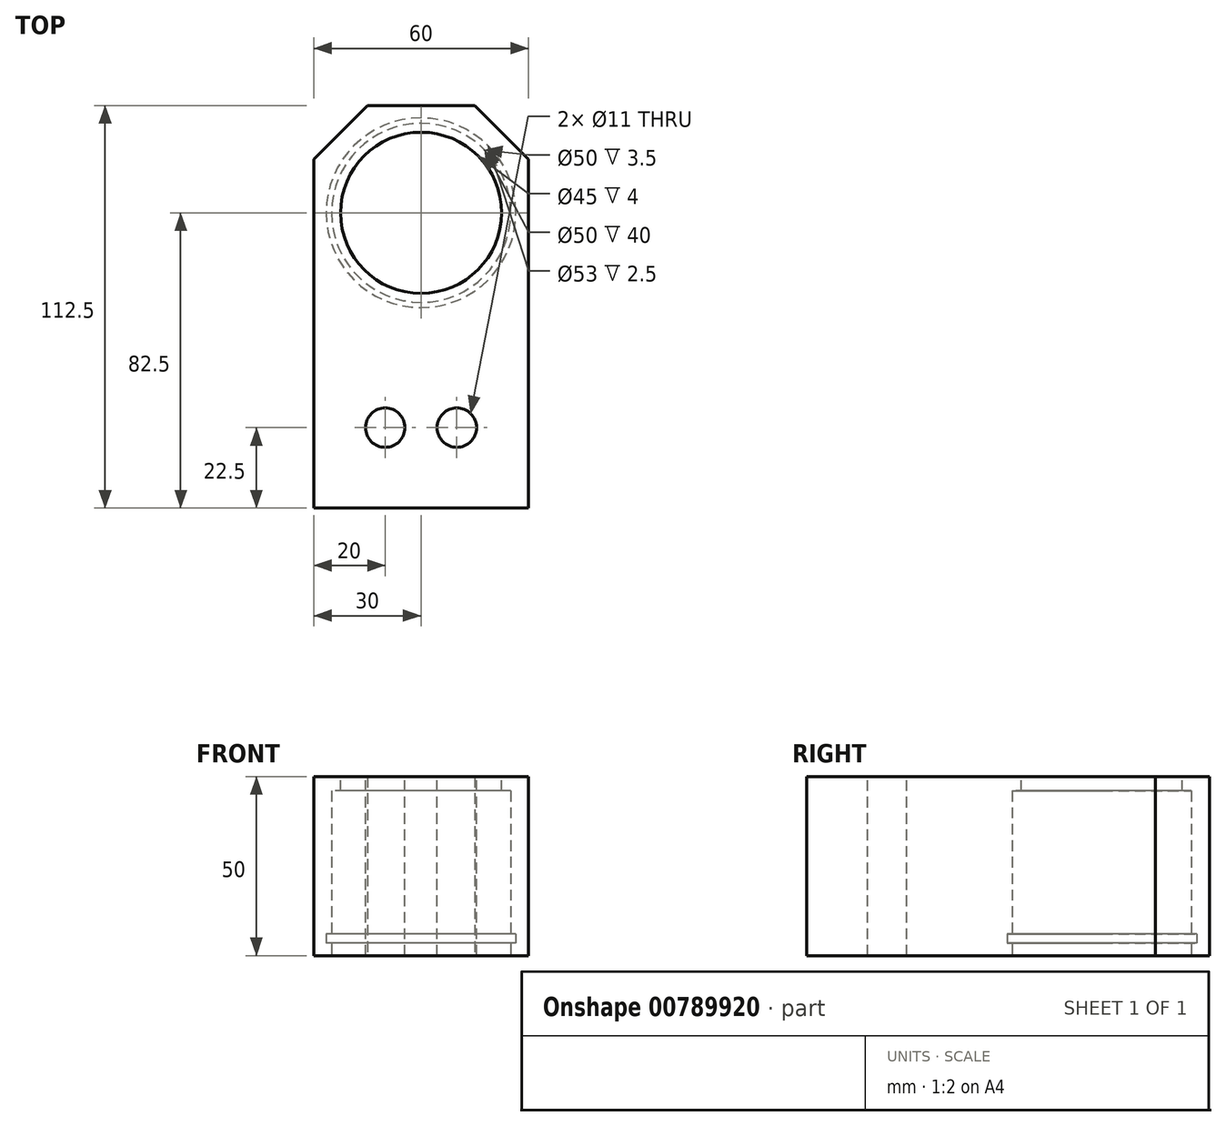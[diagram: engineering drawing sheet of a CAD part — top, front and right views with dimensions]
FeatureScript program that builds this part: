
annotation { "Feature Type Name" : "Feature", "Feature Type Description" : "" }
export const myFeature = defineFeature(function(context is Context, id is Id, definition is map)
    precondition{}
    {
        {
            var Q0;
            Q0=qCreatedBy(makeId("Top.planeOp"),FACE);
            var sketch = newSketch(context, id + "F0", { "sketchPlane" : qUnion([Q0])});
            skLineSegment(sketch, "E0.bottom", {"start": v(-15, 30) * mm, "end": v(15, 30) * mm});
            skLineSegment(sketch, "E0.top", {"start": v(-30, -82.5) * mm, "end": v(30, -82.5) * mm});
            skLineSegment(sketch, "E0.left", {"start": v(-30, 15) * mm, "end": v(-30, -82.5) * mm});
            skLineSegment(sketch, "E0.right", {"start": v(30, 15) * mm, "end": v(30, -82.5) * mm});
            skLineSegment(sketch, "E1", {"start": v(-30, 15) * mm, "end": v(-15, 30) * mm});
            skLineSegment(sketch, "E2.MirrorCS", {"start": v(30, 15) * mm, "end": v(15, 30) * mm});
            skLineSegment(sketch, "E3", {"start": v(-30, -60) * mm, "end": v(30, -60) * mm, "construction": true});
            skPoint(sketch, "E4", {"position": v(-10, -60) * mm});
            skPoint(sketch, "E5", {"position": v(10, -60) * mm});
            skPoint(sketch, "E6", {"position": v(0, 0) * mm});
            skSolve(sketch);
        }
        {
            var Q0;
            Q0=qSketchRegion(id+"F0",true);
            extrude(context, id + "F1", {"entities" : qUnion([Q0]), "depth" : 50 * mm, "offsetDistance" : 25 * mm});
        }
        {
            var Q0;
            Q0=sQuery(id+"F0.wireOp",VERTEX,"E4");
            var Q1;
            Q1=sQuery(id+"F0.wireOp",VERTEX,"E5");
            var Q2;
            Q2=makeQuery(id+"F1.opExtrude","SWEPT_BODY",BODY,{"disambiguationData":[OSD([sQuery(id+"F0.wireOp",EDGE,"E0.bottom"),sQuery(id+"F0.wireOp",EDGE,"E0.top"),sQuery(id+"F0.wireOp",EDGE,"E0.left"),sQuery(id+"F0.wireOp",EDGE,"E0.right"),sQuery(id+"F0.wireOp",EDGE,"E1"),sQuery(id+"F0.wireOp",EDGE,"E2.MirrorCS")])]});
            hole(context, id + "F2", {"style" : HoleStyle.SIMPLE, "endStyle" : HoleEndStyle.THROUGH, "oppositeDirection" : true, "standardTappedOrClearance" : lookupTablePath({ "standard" : "ISO", "fit" : "Normal", "size" : "M10", "type" : "Clearance" }), "standardBlindInLast" : lookupTablePath({ "fit" : "Standard", "standard" : "ISO", "size" : "M10", "type" : "Clearance" }), "holeDiameter" : 11 * mm, "majorDiameter" : 5 * mm, "isTappedThrough" : true, "tappedDepth" : 12 * mm, "tapClearance" : 3, "locations" : qUnion([Q0, Q1]), "scope" : qUnion([Q2]), "startStyle" : HoleStartStyle.PART});
        }
        {
            var Q0;
            Q0=sQuery(id+"F0.wireOp",VERTEX,"E6");
            var Q1;
            Q1=makeQuery(id+"F1.opExtrude","SWEPT_BODY",BODY,{"disambiguationData":[OSD([sQuery(id+"F0.wireOp",EDGE,"E0.bottom"),sQuery(id+"F0.wireOp",EDGE,"E0.top"),sQuery(id+"F0.wireOp",EDGE,"E0.left"),sQuery(id+"F0.wireOp",EDGE,"E0.right"),sQuery(id+"F0.wireOp",EDGE,"E1"),sQuery(id+"F0.wireOp",EDGE,"E2.MirrorCS")])]});
            hole(context, id + "F3", {"style" : HoleStyle.SIMPLE, "endStyle" : HoleEndStyle.THROUGH, "oppositeDirection" : true, "holeDiameter" : 45 * mm, "majorDiameter" : 5 * mm, "isTappedThrough" : true, "tappedDepth" : 12 * mm, "tapClearance" : 3, "locations" : qUnion([Q0]), "scope" : qUnion([Q1]), "startStyle" : HoleStartStyle.PART});
        }
        {
            var Q0;
            Q0=qCreatedBy(makeId("Top.planeOp"),FACE);
            var sketch = newSketch(context, id + "F4", { "sketchPlane" : qUnion([Q0])});
            skCircle(sketch, "E7", {"center": v(0, 0) * mm, "radius": 25 * mm});
            skSolve(sketch);
        }
        {
            var Q0;
            Q0=qSketchRegion(id+"F4",true);
            extrude(context, id + "F5", {"entities" : qUnion([Q0]), "operationType" : NewBodyOperationType.REMOVE, "depth" : 46 * mm, "offsetDistance" : 25 * mm});
        }
        {
            var Q0;
            Q0=qCreatedBy(makeId("Top.planeOp"),FACE);
            var sketch = newSketch(context, id + "F6", { "sketchPlane" : qUnion([Q0])});
            skCircle(sketch, "E8", {"center": v(0, 0) * mm, "radius": 26.5 * mm});
            skSolve(sketch);
        }
        {
            var Q0;
            Q0=qSketchRegion(id+"F6",true);
            extrude(context, id + "F7", {"entities" : qUnion([Q0]), "operationType" : NewBodyOperationType.REMOVE, "depth" : 6 * mm, "offsetDistance" : 25 * mm, "hasSecondDirection" : true, "secondDirectionOppositeDirection" : false, "secondDirectionDepth" : 3.5 * mm});
        }
    });
